# Revit family: QF_BPRO_CCE 54-38_574927
name_source: partatom
category: Sonderausstattung
revit_build: Autodesk Revit 2018 (Build: 20190510_1515(x64)
units: mm (PartAtom-declared; Revit-internal decimal feet)

## family parameters
Arbeitsebenenbasiert = Nein
Beim Laden mit Abzugskörper schneiden = Nein
Bemaßung runder Anschluss = Durchmesser verwenden
Gemeinsam genutzt = Nein
Immer vertikal = Ja
Raumberechnungspunkt = Ja
Teiletyp = Normal

## types (1)
- CCE 54-38
    Artikel Nummer = 574927
    Beschreibung = Tablettspender, offene Ausführung;
max. 530 x 370 mm
ca. 100 Tabletts;
    Beschreibung durch Hersteller analog Leistungsverzeichniskurztext = Abmessungen

Länge:					810 mm
Breite:					555 mm
Höhe:					900 mm


Ausführung

Aufbau
Der Tablettspender besteht komplett aus CNS 18/10. Die Oberfläche ist mikroliert. 
Der Tablettspender ist offen ausgeführt. Die Tabletts werden auf eine Plattform aufgesetzt. Diese ist allseitig aufgekantet (nicht an den Ecken: Reinigung), um das Verrutschen der Tabletts zu vermeiden.
Durch Ein- bzw. Aushängen der Zugfedern kann die Federspannung entsprechend dem Stapelgut reguliert werden, um eine gleichbleibende Ausgabehöhe zu gewährleisten.
Bedienseitig ist ein CNS- Schiebegriff angebracht.
Fahrbar ist der Spender mittels rostfreien Kunststoffrollen (4 Lenkrollen, 2 davon mit Feststeller mit 125 mm ø). Massive Stoßecken aus Kunststoff (Polyamid) an allen vier Ecken schützen vor Beschädigung.


Zubehör/ Optionen

•	Besteckaufsatz mit oder ohne Serviettenspender
•	Weitere Zubehöre und Rollenausführungen siehe Gesamt-Preisliste



Technische Daten

Werkstoff:		CNS 18/10
Gewicht:		31,5 kg
Kapazität:		ca. 100 Tabletts,
		530 x 370 mm
Stapelhöhe:		700 mm
Max. Zuladung:		200 Kg




Besonderheit

•	Veränderung der Federspannung möglich
•	gemäß DIN 18665, Teil 6


Fabrikat

Hersteller:			B.PRO
Modell:				CCE 54/ 38
Best.Nr.			574 927
    Beschreibung durch Hersteller analog Leistungsverzeichnislangtext = Abmessungen

Länge:					810 mm
Breite:					555 mm
Höhe:					900 mm


Ausführung

Aufbau
Der Tablettspender besteht komplett aus CNS 18/10. Die Oberfläche ist mikroliert. 
Der Tablettspender ist offen ausgeführt. Die Tabletts werden auf eine Plattform aufgesetzt. Diese ist allseitig aufgekantet (nicht an den Ecken: Reinigung), um das Verrutschen der Tabletts zu vermeiden.
Durch Ein- bzw. Aushängen der Zugfedern kann die Federspannung entsprechend dem Stapelgut reguliert werden, um eine gleichbleibende Ausgabehöhe zu gewährleisten.
Bedienseitig ist ein CNS- Schiebegriff angebracht.
Fahrbar ist der Spender mittels rostfreien Kunststoffrollen (4 Lenkrollen, 2 davon mit Feststeller mit 125 mm ø). Massive Stoßecken aus Kunststoff (Polyamid) an allen vier Ecken schützen vor Beschädigung.


Zubehör/ Optionen

•	Besteckaufsatz mit oder ohne Serviettenspender
•	Weitere Zubehöre und Rollenausführungen siehe Gesamt-Preisliste



Technische Daten

Werkstoff:		CNS 18/10
Gewicht:		31,5 kg
Kapazität:		ca. 100 Tabletts,
		530 x 370 mm
Stapelhöhe:		700 mm
Max. Zuladung:		200 Kg




Besonderheit

•	Veränderung der Federspannung möglich
•	gemäß DIN 18665, Teil 6


Fabrikat

Hersteller:			B.PRO
Modell:				CCE 54/ 38
Best.Nr.			574 927
    Gerätegewicht Netto = 31.50 kg
    Großküchengerätezuordnung = Ja
    Hersteller = B.PRO GmbH
    Höhe = 900 mm  [stored 2.95276 ft]
    Internetadresse Gerätehersteller = https://www.bpro-solutions.com
    Internetadresse für Ersatzteilliste = https://www.bpro-solutions.com
    Kosten = 1309.4 $
    Länge Gerätebreite = 810 mm
    Länge Tablettträger = 384 mm
    Länge Tragarm = 319 mm
    Material = QF_Metal-Stainless-Steel_general
    Material_Stoßschutz = QF_Rubber-Black-Matt
    Modell = CCE 54-38
    Sockelhöhe = 160 mm  [stored 0.524934 ft]
    Tablettträger OK = 575 mm
    Tiefe = 555 mm  [stored 1.82087 ft]
    Tiefe Tablettträger = 540 mm
    Typenkommentare = Tablettspender offen, quer
    URL = https://www.bpro-solutions.com
    Warnhinweise = Ausführliche Gefahrenhinweise entnehmen Sie der Betriebsanleitung.
    Zubehör = Nein

note: [stored X ft] marks values corroborated as IEEE doubles in the binary element streams (Revit-internal decimal feet)
